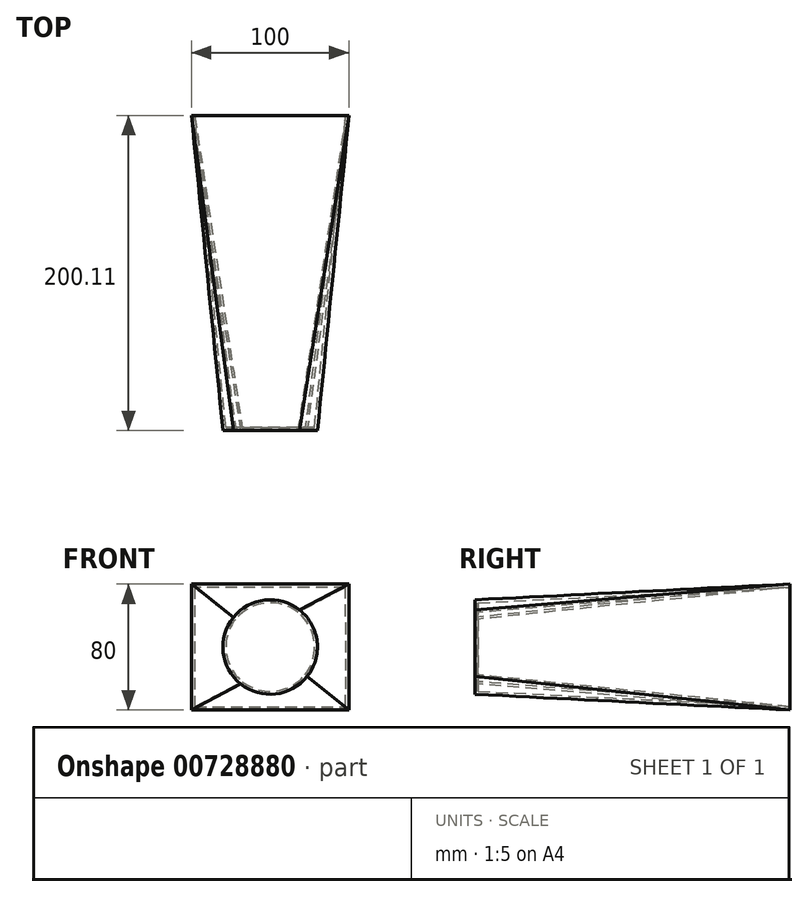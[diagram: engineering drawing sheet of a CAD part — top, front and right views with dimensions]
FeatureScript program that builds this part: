
annotation { "Feature Type Name" : "Feature", "Feature Type Description" : "" }
export const myFeature = defineFeature(function(context is Context, id is Id, definition is map)
    precondition{}
    {
        {
            var Q0;
            Q0=qCreatedBy(makeId("Front.planeOp"),FACE);
            var sketch = newSketch(context, id + "F0", { "sketchPlane" : qUnion([Q0])});
            skLineSegment(sketch, "E0.bottom", {"start": v(50, -40) * mm, "end": v(-50, -40) * mm});
            skLineSegment(sketch, "E0.top", {"start": v(50, 40) * mm, "end": v(-50, 40) * mm});
            skLineSegment(sketch, "E0.left", {"start": v(50, -40) * mm, "end": v(50, 40) * mm});
            skLineSegment(sketch, "E0.right", {"start": v(-50, -40) * mm, "end": v(-50, 40) * mm});
            skPoint(sketch, "E0.middle", {"position": v(0, 0) * mm});
            skSolve(sketch);
        }
        {
            var Q0;
            Q0=qCreatedBy(makeId("Front.planeOp"),FACE);
            cPlane(context, id + "F1", {"entities" : qUnion([Q0]), "cplaneType" : CPlaneType.OFFSET, "offset" : 200 * mm, "width" : 150 * mm, "height" : 150 * mm});
        }
        {
            var Q0;
            Q0=qCreatedBy(id+"F1.planeOp",FACE);
            var sketch = newSketch(context, id + "F2", { "sketchPlane" : qUnion([Q0])});
            skCircle(sketch, "E1", {"center": v(0, 0) * mm, "radius": 30 * mm});
            skSolve(sketch);
        }
        {
            var Q0;
            Q0 = qSketchRegion(id + "F0", true);
            var Q1;
            Q1 = qSketchRegion(id + "F2", true);
            loft(context, id + "F3", {"sheetProfilesArray" : [{ "sheetProfileEntities" : qUnion([Q0]) }, { "sheetProfileEntities" : qUnion([Q1]) }]});
        }
        {
            var Q0;
            Q0=makeQuery(id+"F3.opLoft","CAP_FACE",FACE,{"disambiguationData":[OSD([makeQuery(id+"F0.imprint","IMPRINT",FACE,{"disambiguationData":[TD([[makeQuery(id+"F0.imprint","IMPRINT",EDGE,{"derivedFrom":sQuery(id+"F0.wireOp",EDGE,"E0.bottom")}),-1.0]])]})])],"isStart":true});
            shell(context, id + "F4", {"entities" : qUnion([Q0]), "thickness" : 2 * mm});
        }
    });
